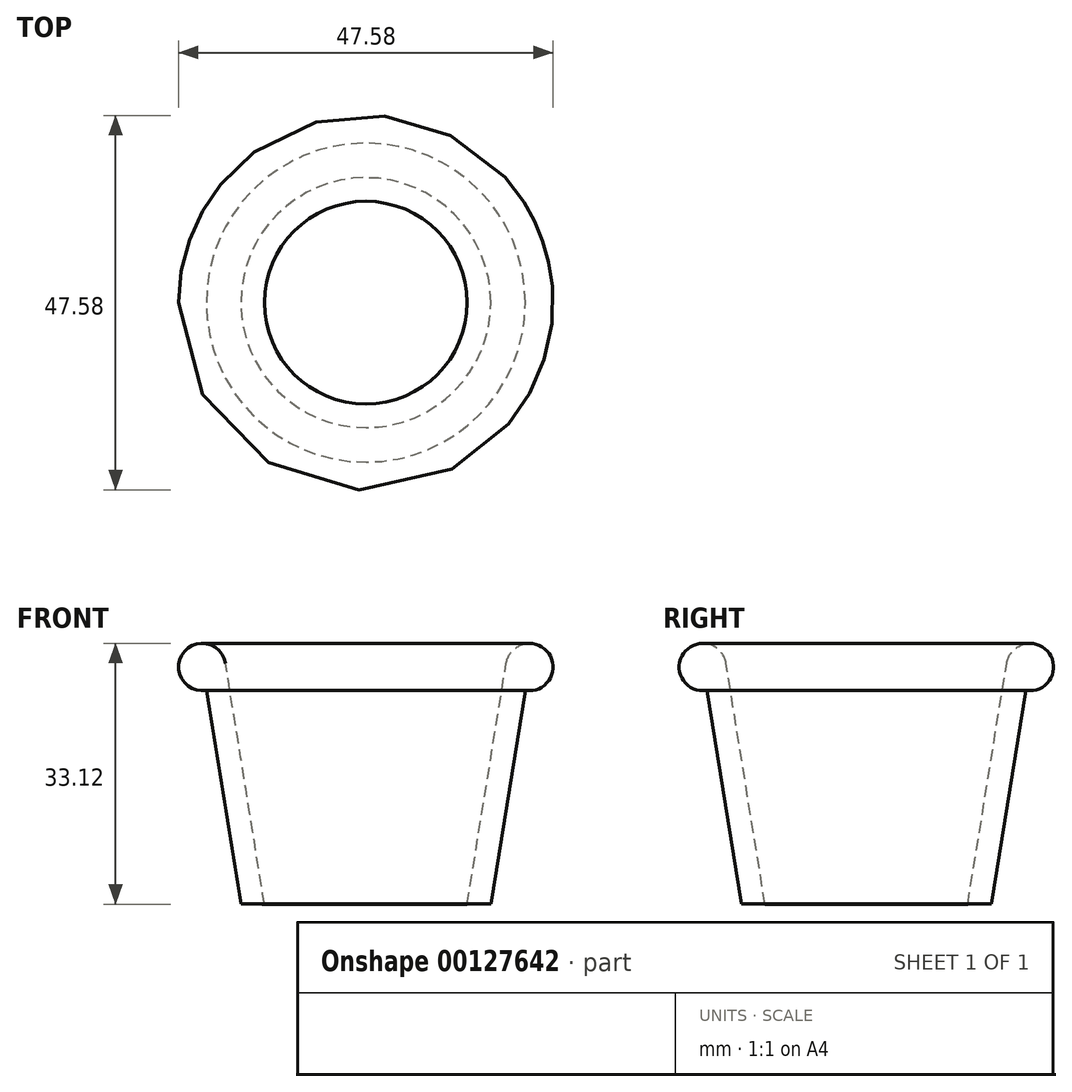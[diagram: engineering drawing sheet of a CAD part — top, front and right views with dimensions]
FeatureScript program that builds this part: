
annotation { "Feature Type Name" : "Feature", "Feature Type Description" : "" }
export const myFeature = defineFeature(function(context is Context, id is Id, definition is map)
    precondition{}
    {
        {
            var Q0;
            Q0=qCreatedBy(makeId("Front.planeOp"),FACE);
            var sketch = newSketch(context, id + "F0", { "sketchPlane" : qUnion([Q0])});
            skPoint(sketch, "E0.second.point", {"position": v(74.92, 3.2) * mm});
            skPoint(sketch, "E0.third.point", {"position": v(37.2, 56.24) * mm});
            skPoint(sketch, "E1.orphan", {"position": v(3.99, 0) * mm});
            skLineSegment(sketch, "E2", {"start": v(0, 0) * mm, "end": v(-15.5, 0) * mm});
            skLineSegment(sketch, "E3", {"start": v(-15.5, 0) * mm, "end": v(-15.5, 56.91) * mm});
            skPoint(sketch, "E4.end.orphan", {"position": v(3.99, 10.64) * mm});
            skPoint(sketch, "E5.visualSharp", {"position": v(7.56, 0) * mm});
            skPoint(sketch, "E6.end.orphan", {"position": v(21.9, 19.17) * mm});
            skArc(sketch, "E7", {"start": v(10.93, 30.15) * mm, "mid": v(10.92, 30.15) * mm, "end": v(10.9, 30.15) * mm});
            skLineSegment(sketch, "E8", {"start": v(3, 14.04) * mm, "end": v(3, 14.17) * mm});
            skLineSegment(sketch, "E9", {"start": v(-2.63, 3.2) * mm, "end": v(2.32, 33.8) * mm});
            skLineSegment(sketch, "E10", {"start": v(-2.63, 3.2) * mm, "end": v(0.37, 3.25) * mm});
            skLineSegment(sketch, "E11", {"start": v(0.37, 3.25) * mm, "end": v(4.76, 30.37) * mm});
            skArc(sketch, "E12", {"start": v(4.76, 30.37) * mm, "mid": v(7.73, 35.07) * mm, "end": v(2.32, 33.8) * mm});
            skSolve(sketch);
        }
        {
            var Q0;
            Q0=makeQuery(id+"F0.imprint","IMPRINT",FACE,{"disambiguationData":[TD([[makeQuery(id+"F0.imprint","IMPRINT",EDGE,{"derivedFrom":sQuery(id+"F0.wireOp",EDGE,"E9")}),-1.0]])]});
            var Q1;
            Q1=sQuery(id+"F0.wireOp",EDGE,"E3");
            revolve(context, id + "F1", {"entities" : qUnion([Q0]), "axis" : qUnion([Q1]), "revolveType" : RevolveType.FULL});
        }
    });
